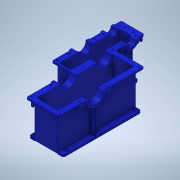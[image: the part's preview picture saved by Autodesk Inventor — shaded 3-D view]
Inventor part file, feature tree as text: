
AUTODESK INVENTOR PART (.ipt)
format: ipt  version: 2020 (Build 240168000, 168)  size: 1,752,064 bytes
history: native  units: mm
features: sketch x82, extrude x68, projected_geometry x43, fillet x26, plane x17, mirror x11, hole x10, other x7, reference x1
ambient origin geometry x8: Origin, YZ Plane, XZ Plane, XY Plane, X Axis, Y Axis, Z Axis, Center Point
bodies: 实体4 (feature_tree)
feature tree (265):
  sketch  "草图1"  dims[d0=41.0mm d1=40.0mm d2=41.0mm d3=8.0mm d4=41.0mm d5=41.0mm d6=40.0mm d7=8.0mm d8=25.0mm d9=71.0mm d10=8.0mm d11=70.0mm d12=190.0mm d13=75.0mm d14=43.0mm d15=8.0mm d16=75.0mm d17=40.0mm d18=31.0mm d19=12.0mm d20=25.0mm d21=10.0mm d22=8.0mm d23=30.0mm d24=5.0mm d25=25.0mm d26=174.0mm d27=91.0mm d28=40.0mm d29=21.0mm d30=71.0mm d31=12.0mm d32=30.0mm d33=30.0mm d34=25.0mm d35=12.0mm d36=30.0mm d37=30.0mm d38=100.0mm d39=40.0mm d40=12.0mm d41=20.0mm d42=70.0mm d43=15.0mm d44=2.0mm d45=31.0mm d56=8.0mm]
  plane  "工作平面6"
  extrude  "拉伸7"  Depth=8.0mm
  plane  "工作平面11"
  extrude  "拉伸35"  Depth=8.0mm
  extrude  "拉伸36"  [1 undecoded]
  extrude  "拉伸37"  Depth=30.0mm
  extrude  "拉伸38"  Depth=30.0mm
  extrude  "拉伸39"  Depth=30.0mm
  extrude  "拉伸40"  Depth=30.0mm
  extrude  "拉伸42"  Depth=10.0mm
  extrude  "拉伸43"  Depth=15.0mm TaperAngle=0.0deg
  plane  "工作平面12"
  mirror  "镜像2"
  extrude  "拉伸44"  Depth=15.0mm TaperAngle=0.0deg
  extrude  "拉伸45"  Depth=10.0mm TaperAngle=0.0deg
  extrude  "拉伸46"  Depth=15.0mm TaperAngle=0.0deg
  extrude  "拉伸47"  Depth=15.0mm TaperAngle=0.0deg
  extrude  "拉伸48"  Depth=15.0mm TaperAngle=0.0deg
  extrude  "拉伸49"  Depth=15.0mm TaperAngle=0.0deg
  extrude  "拉伸50"  Depth=15.0mm TaperAngle=0.0deg
  extrude  "拉伸51"  Depth=15.0mm TaperAngle=0.0deg
  extrude  "拉伸52"  Depth=15.0mm TaperAngle=0.0deg
  extrude  "拉伸53"  Depth=15.0mm TaperAngle=0.0deg
  extrude  "拉伸54"  Depth=25.0mm TaperAngle=0.0deg
  extrude  "拉伸55"  Depth=50.0mm
  extrude  "拉伸56"  Depth=50.0mm
  extrude  "拉伸57"  Depth=12.0mm
  extrude  "拉伸58"  Depth=70.0mm
  extrude  "拉伸59"  Depth=15.0mm TaperAngle=0.0deg
  extrude  "拉伸60"  Depth=68.869mm
  other  "对称面14"
  mirror  "镜像3"
  extrude  "拉伸62"  Depth=3.0mm TaperAngle=0.0deg
  mirror  "镜像4"
  fillet  "圆角1"  Radius=3.0mm
  fillet  "圆角2"  Radius=16.011mm
  extrude  "拉伸63"  Depth=16.153mm TaperAngle=0.0deg
  plane  "工作平面15"
  extrude  "拉伸64"  Depth=13.0mm TaperAngle=0.0deg
  extrude  "拉伸65"  Depth=60.0mm
  extrude  "拉伸66"  Depth=13.0mm TaperAngle=0.0deg
  plane  "工作平面16"
  mirror  "镜像5"
  mirror  "镜像6"
  extrude  "拉伸67"  Depth=13.0mm TaperAngle=0.0deg
  extrude  "拉伸68"  Depth=13.0mm TaperAngle=0.0deg
  extrude  "拉伸69"  Depth=13.0mm TaperAngle=0.0deg
  extrude  "拉伸70"  Depth=13.0mm TaperAngle=0.0deg
  extrude  "拉伸71"  Depth=13.0mm TaperAngle=0.0deg
  fillet  "圆角3"  Radius=13.0mm
  extrude  "拉伸72"  Depth=5.0mm
  fillet  "圆角4"  Radius=5.0mm
  extrude  "拉伸73"  Depth=5.0mm
  extrude  "拉伸74"  Depth=20.0mm
  extrude  "拉伸75"  Depth=28.0mm
  extrude  "拉伸76"  Depth=60.0mm
  extrude  "拉伸77"  Depth=28.0mm
  extrude  "拉伸78"  Depth=5.0mm TaperAngle=0.0deg
  extrude  "拉伸79"  Depth=10.0mm TaperAngle=0.0deg
  extrude  "拉伸80"  Depth=39.485mm
  extrude  "拉伸81"  Depth=18.0mm
  extrude  "拉伸82"  Depth=20.0mm TaperAngle=0.0deg
  extrude  "拉伸83"  Depth=40.0mm
  extrude  "拉伸84"  Depth=12.0mm
  extrude  "拉伸85"  Depth=30.0mm TaperAngle=0.0deg
  extrude  "拉伸86"  Depth=28.0mm
  extrude  "拉伸87"  Depth=16.0mm
  extrude  "拉伸88"  Depth=4.0mm TaperAngle=0.0deg
  extrude  "拉伸89"  Depth=25.307274mm
  fillet  "圆角5"  [1 undecoded]
  extrude  "拉伸90"  Depth=120.0mm
  extrude  "拉伸92"  Depth=4.0mm TaperAngle=0.0deg
  fillet  "圆角8"  Radius=30.0mm
  hole  "孔1"  [1 undecoded]
  extrude  "拉伸93"  Depth=1.0mm
  extrude  "拉伸94"  Depth=1.0mm
  sketch  "草图95"  dims[d363=13.835mm d364=36.0mm d365=28.0mm d366=2.0mm d367=90.0deg d368=41.3mm d369=0.0mm d370=25.307274mm d371=90.0deg]
  hole  "孔3"  [1 undecoded]
  hole  "孔4"  [1 undecoded]
  hole  "孔5"  [1 undecoded]
  plane  "工作平面18"
  plane  "工作平面19"
  extrude  "拉伸95"  Depth=105.0mm
  plane  "工作平面20"
  extrude  "拉伸96"  Depth=72.0mm
  mirror  "镜像7"
  extrude  "拉伸97"  Depth=40.0mm
  extrude  "拉伸98"  Depth=15.0mm
  hole  "孔6"  [1 undecoded]
  sketch  "草图107"  dims[d410=13.835mm d411=36.0mm d412=28.0mm d413=2.0mm d414=90.0deg d415=41.3mm d416=0.0mm d417=175.0mm]
  plane  "工作平面21"
  extrude  "拉伸99"  Depth=2.0mm
  extrude  "拉伸100"  Depth=2.0mm
  hole  "孔7"  [1 undecoded]
  plane  "工作平面22"
  plane  "工作平面23"
  plane  "工作平面24"
  other  "加强筋1"
  mirror  "镜像8"
  other  "加强筋2"
  other  "加强筋3"
  mirror  "镜像9"
  plane  "工作平面25"
  extrude  "拉伸101"  Depth=20.0mm
  hole  "孔8"  [1 undecoded]
  hole  "孔9"  [1 undecoded]
  plane  "工作平面26"
  mirror  "镜像10"
  hole  "孔10"  [1 undecoded]
  hole  "孔11"  [1 undecoded]
  plane  "工作平面27"
  mirror  "镜像11"
  extrude  "拉伸102"  Depth=2.0mm
  extrude  "拉伸103"  Depth=2.0mm
  plane  "工作平面28"
  mirror  "镜像12"
  fillet  "圆角9"  Radius=2.0mm
  fillet  "圆角10"  Radius=2.0mm
  fillet  "圆角11"  Radius=2.0mm
  fillet  "圆角12"  Radius=2.0mm
  fillet  "圆角13"  Radius=2.0mm
  fillet  "圆角14"  Radius=0.5mm
  fillet  "圆角15"  Radius=0.872665mm
  extrude  "拉伸104"  Depth=0.5mm
  fillet  "圆角16"  Radius=0.872665mm
  fillet  "圆角17"  Radius=0.5mm
  fillet  "圆角18"  Radius=0.872665mm
  fillet  "圆角19"  Radius=0.5mm
  fillet  "圆角20"  Radius=0.872665mm
  fillet  "圆角21"  Radius=0.5mm
  fillet  "圆角22"  Radius=0.872665mm
  fillet  "圆角23"  Radius=0.5mm
  fillet  "圆角24"  Radius=0.872665mm
  fillet  "圆角25"  Radius=0.5mm
  fillet  "圆角26"  Radius=0.872665mm
  fillet  "圆角27"  Radius=0.5mm
  fillet  "圆角28"  Radius=0.872665mm
  sketch  "草图9"  dims[d57=8.0mm d58=8.0mm]
  sketch  "草图36"  dims[d59=8.0mm d65=-360.0mm]
  sketch  "草图37"  dims[d66=30.0mm d67=30.0mm]
  sketch  "草图38"  dims[d68=30.0mm d69=30.0mm]
  sketch  "草图39"  dims[d70=30.0mm d71=30.0mm]
  sketch  "草图41"  dims[d72=30.0mm d73=30.0mm]
  sketch  "草图42"  dims[d74=15.0mm d75=0.0mm d139=10.0mm]
  sketch  "草图43"  dims[d140=10.0mm d141=15.0mm d142=0.0mm]
  sketch  "草图44"  dims[d143=15.0mm d144=0.0mm d145=15.0mm d146=0.0mm]
  sketch  "草图45"  dims[d147=10.0mm d148=0.0mm d149=10.0mm d150=0.0mm]
  sketch  "草图46"  dims[d151=10.0mm d152=0.0mm d155=15.0mm d156=0.0mm]
  sketch  "草图47"  dims[d157=15.0mm d158=0.0mm d159=15.0mm d160=0.0mm]
  sketch  "草图48"  dims[d161=15.0mm d162=0.0mm d163=15.0mm d164=0.0mm]
  projected_geometry  "投影回路6"
  sketch  "草图49"  dims[d165=15.0mm d166=0.0mm d167=15.0mm d168=0.0mm]
  sketch  "草图50"  dims[d169=15.0mm d170=0.0mm d171=15.0mm d172=0.0mm]
  sketch  "草图51"  dims[d173=15.0mm d174=0.0mm d175=15.0mm d176=0.0mm]
  sketch  "草图52"  dims[d177=15.0mm d178=0.0mm d179=15.0mm d180=0.0mm]
  sketch  "草图53"  dims[d181=15.0mm d182=0.0mm d183=15.0mm d184=0.0mm]
  sketch  "草图54"  dims[d185=5.0mm d186=0.0mm d187=25.0mm d188=0.0mm]
  sketch  "草图55"  dims[d189=25.807mm d190=0.0mm d191=50.0mm]
  projected_geometry  "投影回路7"
  sketch  "草图56"  dims[d192=46.0mm d193=0.0mm d194=50.0mm]
  projected_geometry  "投影回路8"
  projected_geometry  "投影回路9"
  sketch  "草图57"  dims[d198=50.0mm d199=0.0mm d200=12.0mm]
  projected_geometry  "投影回路10"
  sketch  "草图58"  dims[d201=12.0mm d202=70.0mm]
  projected_geometry  "投影回路11"
  sketch  "草图60"  dims[d203=46.0mm d204=0.0mm d205=15.0mm d206=0.0mm]
  sketch  "草图61"  dims[d207=23.0mm d208=0.0mm d209=68.869mm]
  projected_geometry  "投影回路12"
  sketch  "草图62"  dims[d210=46.0mm d211=0.0mm d212=3.0mm d213=0.0mm d214=3.0mm d215=0.0mm d216=16.011mm d217=0.0mm]
  sketch  "草图63"  dims[d218=3.0mm d219=0.0mm d220=16.153mm d221=0.0mm]
  projected_geometry  "投影回路13"
  sketch  "草图64"  dims[d222=20.0mm d223=13.0mm d224=0.0mm]
  projected_geometry  "投影回路14"
  sketch  "草图65"  dims[d225=12.0mm d226=60.0mm]
  plane  "工作平面17"
  sketch  "草图66"  dims[d227=13.0mm d228=0.0mm d229=13.0mm d230=0.0mm]
  projected_geometry  "投影回路15"
  sketch  "草图67"  dims[d231=13.0mm d232=0.0mm d233=13.0mm d234=0.0mm]
  projected_geometry  "投影回路16"
  sketch  "草图68"  dims[d235=13.0mm d236=0.0mm d237=13.0mm d238=0.0mm]
  projected_geometry  "投影回路17"
  sketch  "草图69"  dims[d239=13.0mm d240=0.0mm d241=13.0mm d242=0.0mm]
  projected_geometry  "投影回路18"
  sketch  "草图70"  dims[d243=13.0mm d244=0.0mm d245=13.0mm d246=0.0mm]
  projected_geometry  "投影回路19"
  sketch  "草图71"  dims[d247=13.0mm d248=0.0mm d249=13.0mm d250=0.0mm d251=13.0mm d252=0.0mm]
  projected_geometry  "投影回路20"
  sketch  "草图72"  dims[d253=5.0mm d254=0.0mm d255=5.0mm d256=5.0mm d257=0.0mm]
  sketch  "草图73"  dims[d258=5.0mm d259=0.0mm d260=5.0mm]
  projected_geometry  "投影回路21"
  sketch  "草图74"  dims[d261=5.0mm d262=0.0mm d263=20.0mm]
  projected_geometry  "投影回路22"
  sketch  "草图75"  dims[d265=5.0mm d266=0.0mm d267=28.0mm]
  projected_geometry  "投影回路23"
  sketch  "草图76"  dims[d269=35.0mm d270=60.0mm]
  projected_geometry  "投影回路24"
  sketch  "草图77"  dims[d271=28.0mm d274=28.0mm]
  projected_geometry  "投影回路25"
  sketch  "草图78"  dims[d275=60.0mm]
  projected_geometry  "投影回路26"
  sketch  "草图79"  dims[d276=20.0mm d277=6.0mm d278=45.0mm d279=2.0mm d280=90.0deg d281=8.0mm d282=20.594885mm d286=5.0mm d287=0.0mm]
  projected_geometry  "投影回路27"
  sketch  "草图80"  dims[d288=20.0mm d289=10.0mm d290=0.0mm]
  projected_geometry  "投影回路28"
  sketch  "草图81"  dims[d291=10.0mm d292=0.0mm]
  projected_geometry  "投影回路29"
  sketch  "草图82"  dims[d293=70.0mm d294=90.0mm d295=120.0mm d296=90.0mm d297=130.0mm d298=140.0mm d299=39.485mm]
  projected_geometry  "投影回路30"
  sketch  "草图83"  dims[d300=22.5mm]
  projected_geometry  "投影回路31"
  projected_geometry  "投影回路32"
  sketch  "草图84"  dims[d323=13.5mm d324=6.0mm d325=26.0mm d326=2.0mm d327=90.0deg d328=8.0mm d329=20.594885mm]
  projected_geometry  "投影回路33"
  sketch  "草图85"  dims[d330=13.5mm d331=6.0mm d332=26.0mm d333=2.0mm d334=90.0deg d335=8.0mm d336=20.594885mm d337=18.0mm]
  projected_geometry  "投影回路34"
  sketch  "草图86"  dims[d338=110.0mm]
  projected_geometry  "投影回路35"
  projected_geometry  "投影回路36"
  sketch  "草图87"  dims[d339=10.0mm d340=6.0mm d341=26.0mm d342=2.0mm d343=90.0deg d344=8.0mm d345=20.594885mm d346=20.0mm d347=0.0mm]
  sketch  "草图88"  dims[d348=-30.0mm d349=40.0mm]
  sketch  "草图89"  dims[d350=6.0mm d351=12.0mm]
  projected_geometry  "投影回路37"
  projected_geometry  "投影回路38"
  projected_geometry  "投影回路39"
  projected_geometry  "投影回路40"
  sketch  "草图90"  dims[d352=20.0mm d353=30.0mm d354=0.0mm]
  sketch  "草图92"  dims[d355=30.0mm d356=0.0mm d357=28.0mm]
  projected_geometry  "投影回路42"
  sketch  "草图93"  dims[d358=5.0mm d359=16.0mm]
  sketch  "草图94"  dims[d360=38.0mm d361=4.0mm d362=0.0mm]
  projected_geometry  "投影回路43"
  projected_geometry  "投影回路44"
  sketch  "草图98"  dims[d372=35.0mm d373=120.0mm]
  sketch  "草图99"  dims[d374=4.0mm d375=0.0mm d376=4.0mm d377=0.0mm]
  sketch  "草图100"  dims[d378=13.835mm d379=32.0mm d380=20.0mm d381=2.0mm d382=90.0deg d383=41.3mm d384=0.0mm d386=30.0mm]
  sketch  "草图101"  dims[d387=30.0mm d388=30.0mm]
  projected_geometry  "投影回路45"
  sketch  "草图102"  dims[d389=30.0mm]
  projected_geometry  "投影回路46"
  sketch  "草图104"  dims[d390=1.0mm d391=9.0mm d392=0.0mm d393=0.0mm d394=1.0mm d395=1.0mm d396=1.0mm]
  sketch  "草图105"  dims[d397=9.0mm d398=0.0mm d399=0.0mm d400=1.0mm d401=1.0mm d402=1.0mm]
  sketch  "草图106"  dims[d403=9.0mm d404=0.0mm d405=0.0mm d406=1.0mm d407=1.0mm d408=4.0mm d409=0.0mm]
  sketch  "草图108"  dims[d418=60.0mm d420=360.0deg]
  sketch  "草图109"  dims[d422=8.376mm d423=15.0mm d424=4.0mm d425=2.0mm d426=90.0deg d427=18.0mm d428=20.594885mm d429=165.0mm]
  projected_geometry  "投影回路48"
  sketch  "草图110"  dims[d430=60.0mm d432=360.0deg]
  sketch  "草图111"  dims[d434=8.376mm d435=15.0mm d436=4.0mm d437=2.0mm d438=90.0deg d439=18.0mm d440=20.594885mm d441=105.0mm]
  sketch  "草图112"  dims[d442=60.0mm d444=360.0deg]
  sketch  "草图113"  dims[d446=8.376mm d447=15.0mm d448=4.0mm d449=2.0mm d450=90.0deg d451=18.0mm d452=20.594885mm d453=72.0mm]
  sketch  "草图114"  dims[d454=10.0mm d455=0.0mm d456=40.0mm]
  sketch  "草图115"  dims[d457=10.0mm d458=15.0mm]
  sketch  "草图116"  dims[d459=20.0mm d460=0.0mm d461=19.0mm]
  projected_geometry  "投影回路49"
  sketch  "草图117"  dims[d462=19.0mm d463=2.0mm]
  sketch  "草图118"  dims[d464=12.0mm d465=2.0mm]
  sketch  "草图119"  dims[d466=2.0mm d467=1.0mm]
  reference  "参考1"
  sketch  "草图120"  dims[d468=25.0mm d469=0.0mm d470=20.0mm]
  sketch  "草图121"  dims[d471=20.0mm d472=12.0mm d473=20.0mm d474=2.0mm d475=2.0mm d476=2.0mm d477=2.0mm d478=2.0mm d479=2.0mm d480=2.0mm d481=2.0mm d482=2.0mm d78=0.5mm d79=0.872665mm d80=0.5mm d81=0.872665mm d106=0.5mm d107=0.872665mm d108=0.5mm d109=0.872665mm d111=0.5mm d112=0.872665mm d113=0.5mm d114=0.872665mm d126=0.5mm d127=0.872665mm d128=0.5mm d129=0.872665mm]
  projected_geometry  "投影回路50"
  other  "<userpath>\Desktop\111111\Workspace\cpz assemble.iam"
  other  "cpz assemble.iam"
  other  "垫片1:2"
note: 12 required parameter values undecoded (feature->parameter linkage not recoverable at this tier; creation-order binding heuristic only, values carry confidence <= 0.55)
